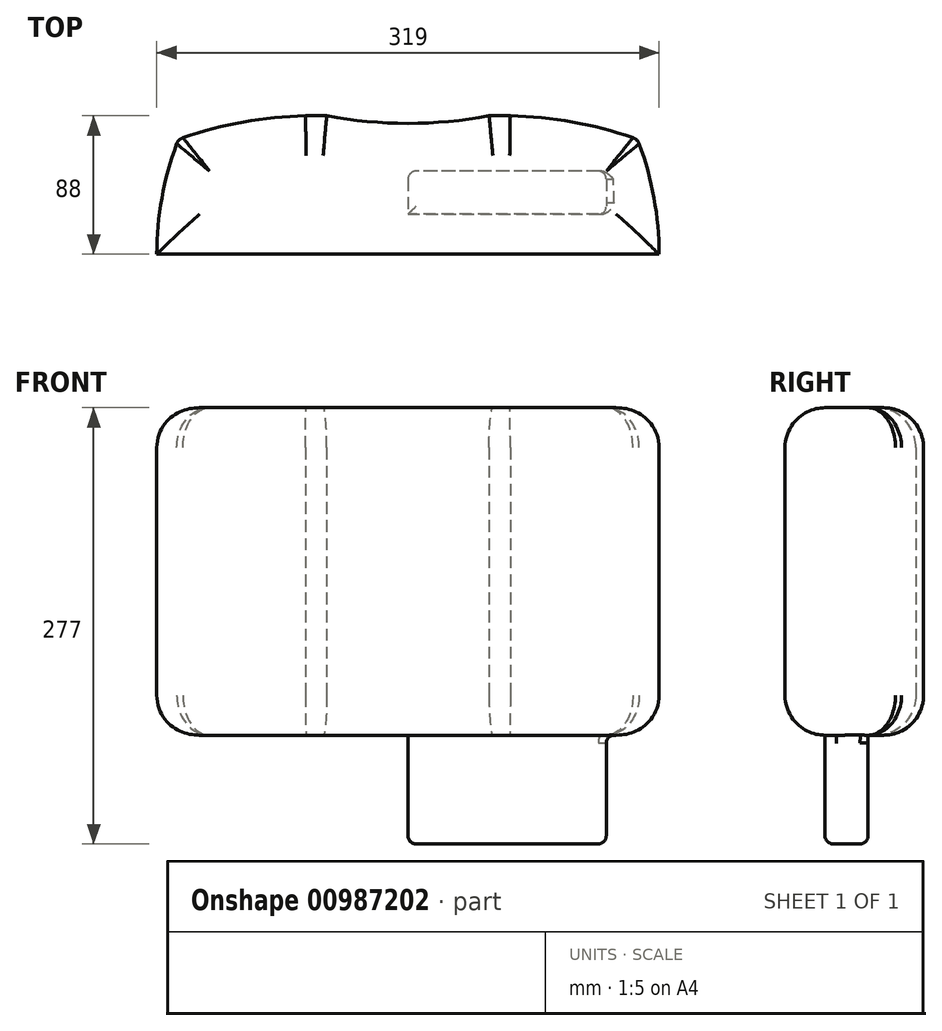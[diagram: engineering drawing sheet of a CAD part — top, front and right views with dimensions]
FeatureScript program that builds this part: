
annotation { "Feature Type Name" : "Feature", "Feature Type Description" : "" }
export const myFeature = defineFeature(function(context is Context, id is Id, definition is map)
    precondition{}
    {
        {
            var Q0;
            Q0=qCreatedBy(makeId("Top.planeOp"),FACE);
            var sketch = newSketch(context, id + "F0", { "sketchPlane" : qUnion([Q0])});
            skLineSegment(sketch, "E0.bottom", {"start": v(-159.5, 96.1) * mm, "end": v(-139.18, 96.1) * mm});
            skLineSegment(sketch, "E0.left", {"start": v(-159.5, 96.1) * mm, "end": v(-159.5, 8.1) * mm});
            skLineSegment(sketch, "E0.right", {"start": v(159.5, 96.1) * mm, "end": v(159.5, 8.1) * mm});
            skArc(sketch, "E1", {"start": v(-146.82, 78.3) * mm, "mid": v(-156.3, 43.76) * mm, "end": v(-159.5, 8.1) * mm});
            skArc(sketch, "E2", {"start": v(159.5, 8.1) * mm, "mid": v(156.3, 43.76) * mm, "end": v(146.82, 78.3) * mm});
            skArc(sketch, "E3", {"start": v(-51.55, 96.1) * mm, "mid": v(0, 91.22) * mm, "end": v(51.55, 96.1) * mm});
            skArc(sketch, "E4", {"start": v(-51.55, 96.1) * mm, "mid": v(-97.86, 93.16) * mm, "end": v(-142.93, 82.08) * mm});
            skArc(sketch, "E5", {"start": v(142.93, 82.08) * mm, "mid": v(97.87, 93.16) * mm, "end": v(51.55, 96.1) * mm});
            skLineSegment(sketch, "E6", {"start": v(-159.5, 8.1) * mm, "end": v(200.05, 8.1) * mm});
            skPoint(sketch, "E7.orphan", {"position": v(-159.5, 75.77) * mm});
            skPoint(sketch, "E8.orphan", {"position": v(-139.18, 96.1) * mm});
            skPoint(sketch, "E9.orphan", {"position": v(139.18, 96.1) * mm});
            skPoint(sketch, "E10.orphan", {"position": v(159.5, 75.77) * mm});
            skLineSegment(sketch, "E11.trimOffspring", {"start": v(139.18, 96.1) * mm, "end": v(159.5, 96.1) * mm});
            skLineSegment(sketch, "E12.trimOffspring", {"start": v(51.55, 96.1) * mm, "end": v(65, 96.1) * mm});
            skLineSegment(sketch, "E13.trimOffspring", {"start": v(-65, 96.1) * mm, "end": v(-51.55, 96.1) * mm});
            skPoint(sketch, "E14.visualSharp", {"position": v(-145.75, 81.1) * mm});
            skArc(sketch, "E14.filletArc", {"start": v(-142.93, 82.08) * mm, "mid": v(-145.3, 80.63) * mm, "end": v(-146.82, 78.3) * mm});
            skPoint(sketch, "E15.visualSharp", {"position": v(145.75, 81.1) * mm});
            skArc(sketch, "E15.filletArc", {"start": v(146.82, 78.3) * mm, "mid": v(145.3, 80.63) * mm, "end": v(142.93, 82.08) * mm});
            skArc(sketch, "E16.MirrorCS", {"start": v(-142.93, -65.9) * mm, "mid": v(-145.3, -64.44) * mm, "end": v(-146.82, -62.11) * mm});
            skArc(sketch, "E17.MirrorCS", {"start": v(146.82, -62.11) * mm, "mid": v(145.3, -64.44) * mm, "end": v(142.93, -65.9) * mm});
            skLineSegment(sketch, "E18.MirrorCS", {"start": v(51.55, -79.9) * mm, "end": v(65, -79.9) * mm});
            skPoint(sketch, "E19.MirrorP", {"position": v(-139.18, -79.9) * mm});
            skPoint(sketch, "E20.MirrorP", {"position": v(145.75, -64.92) * mm});
            skPoint(sketch, "E21.MirrorP", {"position": v(-159.5, -59.59) * mm});
            skArc(sketch, "E22.MirrorCS", {"start": v(-35.75, -77.37) * mm, "mid": v(0, -75.04) * mm, "end": v(35.75, -77.37) * mm});
            skPoint(sketch, "E23.MirrorP", {"position": v(-145.75, -64.92) * mm});
            skArc(sketch, "E24.MirrorCS", {"start": v(142.93, -65.9) * mm, "mid": v(119.35, -72.76) * mm, "end": v(95.23, -77.37) * mm});
            skPoint(sketch, "E25.MirrorP", {"position": v(139.18, -79.9) * mm});
            skArc(sketch, "E26.MirrorCS", {"start": v(-146.82, -62.11) * mm, "mid": v(-156.3, -27.58) * mm, "end": v(-159.5, 8.1) * mm});
            skPoint(sketch, "E27.MirrorP", {"position": v(159.5, -59.59) * mm});
            skArc(sketch, "E28.MirrorCS", {"start": v(159.5, 8.1) * mm, "mid": v(156.3, -27.58) * mm, "end": v(146.82, -62.11) * mm});
            skLineSegment(sketch, "E29", {"start": v(-162.16, -77.37) * mm, "end": v(-35.75, -77.37) * mm});
            skArc(sketch, "E30.trimOffspring", {"start": v(-95.23, -77.37) * mm, "mid": v(-119.35, -72.76) * mm, "end": v(-142.93, -65.9) * mm});
            skPoint(sketch, "E31.MirrorCS.end.orphan", {"position": v(-51.55, -79.9) * mm});
            skPoint(sketch, "E31.MirrorCS.start.orphan", {"position": v(-65, -79.9) * mm});
            skLineSegment(sketch, "E32.trimOffspring", {"start": v(35.75, -77.37) * mm, "end": v(204.74, -77.37) * mm});
            skSolve(sketch);
        }
        {
            var Q0;
            Q0=makeQuery(id+"F0.imprint","IMPRINT",FACE,{"disambiguationData":[TD([[makeQuery(id+"F0.imprint","IMPRINT",EDGE,{"derivedFrom":sQuery(id+"F0.wireOp",EDGE,"E16.MirrorCS")}),-1.0]])]});
            var Q1;
            {var subQ4=sQuery(id+"F0.wireOp",EDGE,"E1");Q1=makeQuery(id+"F0.imprint","IMPRINT",FACE,{"disambiguationData":[TD([[makeQuery(id+"F0.imprint","IMPRINT",EDGE,{"derivedFrom":subQ4}),1.0]])]});}
            extrude(context, id + "F1", {"entities" : qUnion([Q0, Q1]), "depth" : 208 * mm, "offsetDistance" : 25.4 * mm});
        }
        {
            var Q0;
            Q0=makeQuery(id+"F1.opExtrude","CAP_FACE",FACE,{"disambiguationData":[OSD([sQuery(id+"F0.wireOp",EDGE,"E1"),sQuery(id+"F0.wireOp",EDGE,"E2"),sQuery(id+"F0.wireOp",EDGE,"E3"),sQuery(id+"F0.wireOp",EDGE,"E4"),sQuery(id+"F0.wireOp",EDGE,"E5"),sQuery(id+"F0.wireOp",EDGE,"E12.trimOffspring"),sQuery(id+"F0.wireOp",EDGE,"E13.trimOffspring"),sQuery(id+"F0.wireOp",EDGE,"E14.filletArc"),sQuery(id+"F0.wireOp",EDGE,"E15.filletArc"),sQuery(id+"F0.wireOp",EDGE,"E16.MirrorCS"),sQuery(id+"F0.wireOp",EDGE,"E17.MirrorCS"),sQuery(id+"F0.wireOp",EDGE,"E22.MirrorCS"),sQuery(id+"F0.wireOp",EDGE,"E24.MirrorCS"),sQuery(id+"F0.wireOp",EDGE,"E26.MirrorCS"),sQuery(id+"F0.wireOp",EDGE,"E28.MirrorCS"),sQuery(id+"F0.wireOp",EDGE,"E29"),sQuery(id+"F0.wireOp",EDGE,"E30.trimOffspring"),sQuery(id+"F0.wireOp",EDGE,"E32.trimOffspring")])],"isStart":true});
            var Q1;
            Q1=makeQuery(id+"F1.opExtrude","CAP_FACE",FACE,{"disambiguationData":[OSD([sQuery(id+"F0.wireOp",EDGE,"E1"),sQuery(id+"F0.wireOp",EDGE,"E2"),sQuery(id+"F0.wireOp",EDGE,"E3"),sQuery(id+"F0.wireOp",EDGE,"E4"),sQuery(id+"F0.wireOp",EDGE,"E5"),sQuery(id+"F0.wireOp",EDGE,"E12.trimOffspring"),sQuery(id+"F0.wireOp",EDGE,"E13.trimOffspring"),sQuery(id+"F0.wireOp",EDGE,"E14.filletArc"),sQuery(id+"F0.wireOp",EDGE,"E15.filletArc"),sQuery(id+"F0.wireOp",EDGE,"E16.MirrorCS"),sQuery(id+"F0.wireOp",EDGE,"E17.MirrorCS"),sQuery(id+"F0.wireOp",EDGE,"E22.MirrorCS"),sQuery(id+"F0.wireOp",EDGE,"E24.MirrorCS"),sQuery(id+"F0.wireOp",EDGE,"E26.MirrorCS"),sQuery(id+"F0.wireOp",EDGE,"E28.MirrorCS"),sQuery(id+"F0.wireOp",EDGE,"E29"),sQuery(id+"F0.wireOp",EDGE,"E30.trimOffspring"),sQuery(id+"F0.wireOp",EDGE,"E32.trimOffspring")])],"isStart":false});
            fillet(context, id + "F2", {"entities" : qUnion([Q0, Q1]), "radius" : 25.4 * mm, "tangentPropagation" : true, "allowEdgeOverflow" : false});
        }
        {
            var Q0;
            Q0=makeQuery(id+"F1.opExtrude","CAP_FACE",FACE,{"disambiguationData":[OSD([sQuery(id+"F0.wireOp",EDGE,"E1"),sQuery(id+"F0.wireOp",EDGE,"E2"),sQuery(id+"F0.wireOp",EDGE,"E3"),sQuery(id+"F0.wireOp",EDGE,"E4"),sQuery(id+"F0.wireOp",EDGE,"E5"),sQuery(id+"F0.wireOp",EDGE,"E12.trimOffspring"),sQuery(id+"F0.wireOp",EDGE,"E13.trimOffspring"),sQuery(id+"F0.wireOp",EDGE,"E14.filletArc"),sQuery(id+"F0.wireOp",EDGE,"E15.filletArc"),sQuery(id+"F0.wireOp",EDGE,"E16.MirrorCS"),sQuery(id+"F0.wireOp",EDGE,"E17.MirrorCS"),sQuery(id+"F0.wireOp",EDGE,"E22.MirrorCS"),sQuery(id+"F0.wireOp",EDGE,"E24.MirrorCS"),sQuery(id+"F0.wireOp",EDGE,"E26.MirrorCS"),sQuery(id+"F0.wireOp",EDGE,"E28.MirrorCS"),sQuery(id+"F0.wireOp",EDGE,"E29"),sQuery(id+"F0.wireOp",EDGE,"E30.trimOffspring"),sQuery(id+"F0.wireOp",EDGE,"E32.trimOffspring")])],"isStart":true});
            var sketch = newSketch(context, id + "F3", { "sketchPlane" : qUnion([Q0])});
            skLineSegment(sketch, "E33.bottom", {"start": v(125.97, -60.85) * mm, "end": v(0, -60.85) * mm});
            skLineSegment(sketch, "E33.top", {"start": v(125.97, 44.23) * mm, "end": v(0, 44.23) * mm});
            skLineSegment(sketch, "E33.left", {"start": v(125.97, -60.85) * mm, "end": v(125.97, 44.23) * mm});
            skLineSegment(sketch, "E33.right", {"start": v(0, -60.85) * mm, "end": v(0, 44.23) * mm});
            skSolve(sketch);
        }
        {
            var Q0;
            Q0=makeQuery(id+"F3.imprint","IMPRINT",FACE,{"disambiguationData":[TD([[makeQuery(id+"F3.imprint","IMPRINT",EDGE,{"derivedFrom":sQuery(id+"F3.wireOp",EDGE,"E33.bottom")}),-1.0]])]});
            extrude(context, id + "F4", {"entities" : qUnion([Q0]), "operationType" : NewBodyOperationType.ADD, "depth" : 69 * mm, "offsetDistance" : 25.4 * mm});
        }
        {
            var Q0;
            Q0=makeQuery(id+"F4.opExtrude","CAP_EDGE",EDGE,{"disambiguationData":[OSD([sQuery(id+"F3.wireOp",EDGE,"E33.bottom")])],"isStart":true});
            var Q1;
            Q1=makeQuery(id+"F4.opExtrude","CAP_EDGE",EDGE,{"disambiguationData":[OSD([sQuery(id+"F3.wireOp",EDGE,"E33.right")])],"isStart":true});
            var Q2;
            Q2=makeQuery(id+"F4.opExtrude","CAP_EDGE",EDGE,{"disambiguationData":[OSD([sQuery(id+"F3.wireOp",EDGE,"E33.left")])],"isStart":true});
            fillet(context, id + "F5", {"entities" : qUnion([Q0, Q1, Q2]), "radius" : 5.08 * mm, "tangentPropagation" : true, "allowEdgeOverflow" : false});
        }
        {
            var Q0;
            Q0=makeQuery(id+"F4.opExtrude","CAP_FACE",FACE,{"disambiguationData":[OSD([sQuery(id+"F3.wireOp",EDGE,"E33.bottom"),sQuery(id+"F3.wireOp",EDGE,"E33.top"),sQuery(id+"F3.wireOp",EDGE,"E33.left"),sQuery(id+"F3.wireOp",EDGE,"E33.right")])],"isStart":false});
            var Q1;
            Q1=makeQuery(id+"F4.opExtrude","SWEPT_EDGE",EDGE,{"disambiguationData":[OSD([sQuery(id+"F0.wireOp",EDGE,"E1"),sQuery(id+"F0.wireOp",EDGE,"E2"),sQuery(id+"F0.wireOp",EDGE,"E3"),sQuery(id+"F0.wireOp",EDGE,"E4"),sQuery(id+"F0.wireOp",EDGE,"E5"),sQuery(id+"F0.wireOp",EDGE,"E12.trimOffspring"),sQuery(id+"F0.wireOp",EDGE,"E13.trimOffspring"),sQuery(id+"F0.wireOp",EDGE,"E14.filletArc"),sQuery(id+"F0.wireOp",EDGE,"E15.filletArc"),sQuery(id+"F0.wireOp",EDGE,"E16.MirrorCS"),sQuery(id+"F0.wireOp",EDGE,"E17.MirrorCS"),sQuery(id+"F0.wireOp",EDGE,"E22.MirrorCS"),sQuery(id+"F0.wireOp",EDGE,"E24.MirrorCS"),sQuery(id+"F0.wireOp",EDGE,"E26.MirrorCS"),sQuery(id+"F0.wireOp",EDGE,"E28.MirrorCS"),sQuery(id+"F0.wireOp",EDGE,"E29"),sQuery(id+"F0.wireOp",EDGE,"E30.trimOffspring"),sQuery(id+"F0.wireOp",EDGE,"E32.trimOffspring"),sQuery(id+"F3.wireOp",EDGE,"E33.bottom"),sQuery(id+"F3.wireOp",EDGE,"E33.left")])]});
            var Q2;
            Q2=makeQuery(id+"F4.opExtrude","SWEPT_EDGE",EDGE,{"disambiguationData":[OSD([sQuery(id+"F3.wireOp",EDGE,"E33.top"),sQuery(id+"F3.wireOp",EDGE,"E33.left")])]});
            var Q3;
            Q3=makeQuery(id+"F4.opExtrude","SWEPT_EDGE",EDGE,{"disambiguationData":[OSD([sQuery(id+"F3.wireOp",EDGE,"E33.top"),sQuery(id+"F3.wireOp",EDGE,"E33.right")])]});
            fillet(context, id + "F6", {"entities" : qUnion([Q0, Q1, Q2, Q3]), "radius" : 5.08 * mm, "tangentPropagation" : true, "allowEdgeOverflow" : false});
        }
    });
